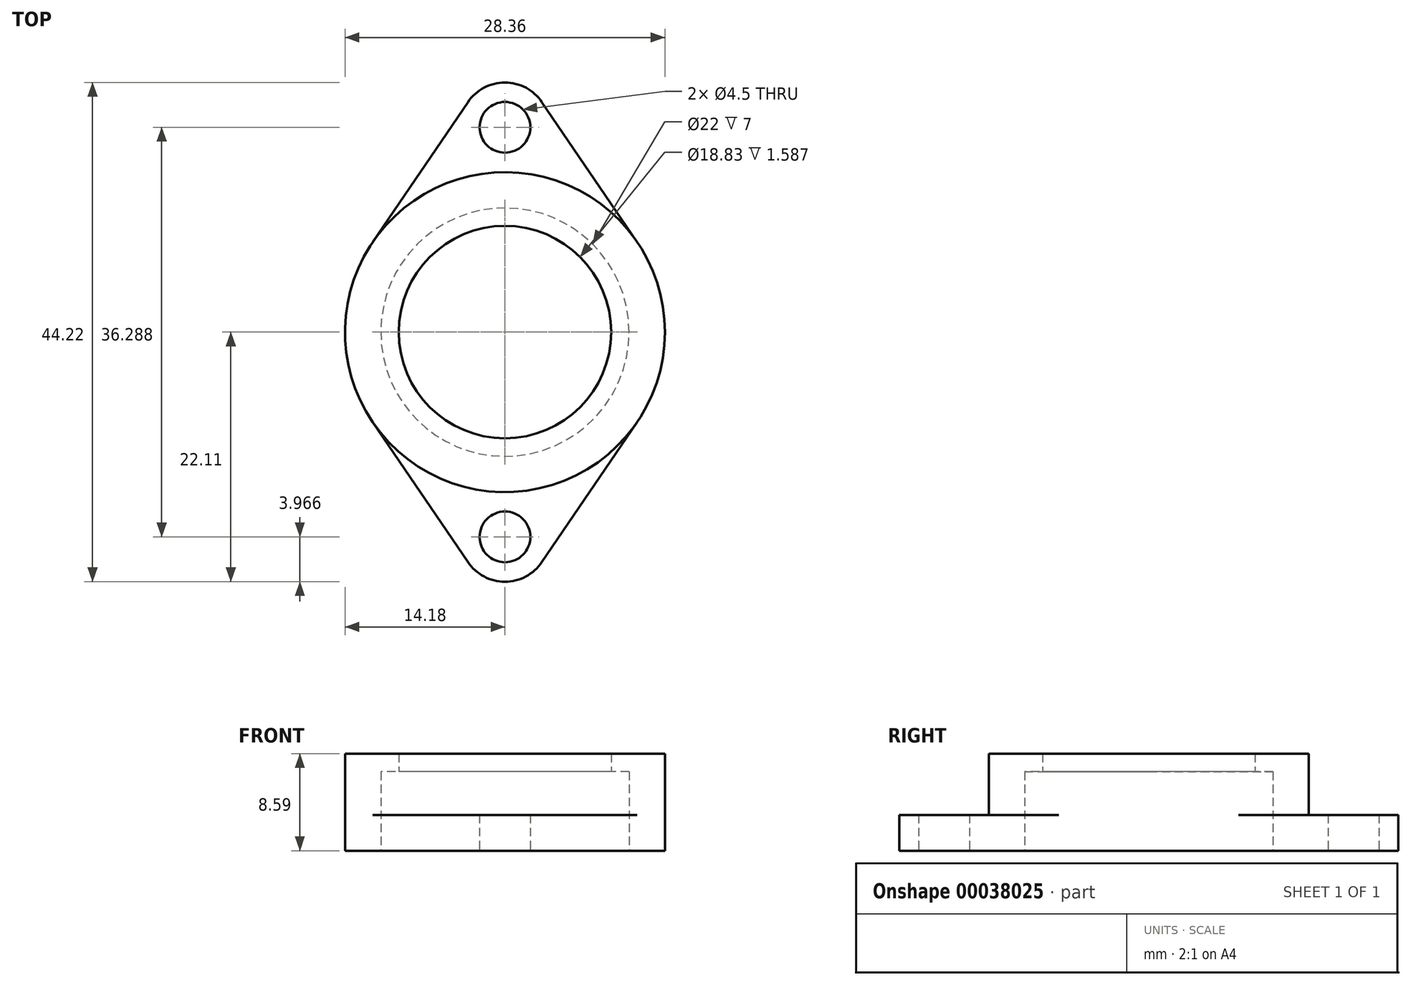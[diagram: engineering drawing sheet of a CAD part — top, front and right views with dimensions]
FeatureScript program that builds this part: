
annotation { "Feature Type Name" : "Feature", "Feature Type Description" : "" }
export const myFeature = defineFeature(function(context is Context, id is Id, definition is map)
    precondition{}
    {
        {
            var Q0;
            Q0=qCreatedBy(makeId("Top.planeOp"),FACE);
            var sketch = newSketch(context, id + "F0", { "sketchPlane" : qUnion([Q0])});
            skCircle(sketch, "E0", {"center": v(0, 0) * mm, "radius": 11 * mm});
            skArc(sketch, "E1", {"start": v(11.72, -7.97) * mm, "mid": v(14.18, 0) * mm, "end": v(11.72, 7.97) * mm});
            skArc(sketch, "E2", {"start": v(-11.72, 7.97) * mm, "mid": v(-14.18, 0) * mm, "end": v(-11.72, -7.97) * mm});
            skLineSegment(sketch, "E3", {"start": v(0, 18.14) * mm, "end": v(0, -18.14) * mm, "construction": true});
            skLineSegment(sketch, "E4", {"start": v(0, -18.14) * mm, "end": v(0, -18.14) * mm});
            skLineSegment(sketch, "E5", {"start": v(-3.97, 18.14) * mm, "end": v(3.97, 18.14) * mm, "construction": true});
            skLineSegment(sketch, "E6", {"start": v(-3.97, -18.14) * mm, "end": v(3.97, -18.14) * mm, "construction": true});
            skArc(sketch, "E7", {"start": v(-3.97, 18.14) * mm, "mid": v(0, 14.18) * mm, "end": v(3.97, 18.14) * mm, "construction": true});
            skArc(sketch, "E8", {"start": v(11.72, 7.97) * mm, "mid": v(0, 14.18) * mm, "end": v(-11.72, 7.97) * mm, "construction": true});
            skArc(sketch, "E9", {"start": v(3.28, 20.38) * mm, "mid": v(0, 22.11) * mm, "end": v(-3.28, 20.38) * mm});
            skLineSegment(sketch, "E10", {"start": v(-3.28, 20.38) * mm, "end": v(-11.72, 7.97) * mm});
            skArc(sketch, "E11", {"start": v(-3.28, 20.38) * mm, "mid": v(-3.8, 19.31) * mm, "end": v(-3.97, 18.14) * mm, "construction": true});
            skArc(sketch, "E12", {"start": v(3.97, 18.14) * mm, "mid": v(3.8, 19.31) * mm, "end": v(3.28, 20.38) * mm, "construction": true});
            skLineSegment(sketch, "E13", {"start": v(3.28, 20.38) * mm, "end": v(11.72, 7.97) * mm});
            skLineSegment(sketch, "E14", {"start": v(-11.72, -7.97) * mm, "end": v(-3.28, -20.38) * mm});
            skLineSegment(sketch, "E15", {"start": v(11.72, -7.97) * mm, "end": v(3.28, -20.38) * mm});
            skArc(sketch, "E16", {"start": v(-3.97, -18.14) * mm, "mid": v(-3.8, -19.31) * mm, "end": v(-3.28, -20.38) * mm, "construction": true});
            skArc(sketch, "E17", {"start": v(3.28, -20.38) * mm, "mid": v(3.8, -19.31) * mm, "end": v(3.97, -18.14) * mm, "construction": true});
            skArc(sketch, "E18", {"start": v(-3.28, -20.38) * mm, "mid": v(0, -22.11) * mm, "end": v(3.28, -20.38) * mm});
            skCircle(sketch, "E19", {"center": v(0, 18.14) * mm, "radius": 2.25 * mm});
            skCircle(sketch, "E20", {"center": v(0, -18.14) * mm, "radius": 2.25 * mm});
            skSolve(sketch);
        }
        {
            var Q0;
            Q0 = qSketchRegion(id + "F0", true);
            extrude(context, id + "F1", {"entities" : qUnion([Q0]), "depth" : 3.17 * mm});
        }
        {
            var Q0;
            Q0=makeQuery(id+"F1.opExtrude","CAP_FACE",FACE,{"disambiguationData":[OSD([sQuery(id+"F0.wireOp",EDGE,"E0"),sQuery(id+"F0.wireOp",EDGE,"E1"),sQuery(id+"F0.wireOp",EDGE,"E2"),sQuery(id+"F0.wireOp",EDGE,"E9"),sQuery(id+"F0.wireOp",EDGE,"E10"),sQuery(id+"F0.wireOp",EDGE,"E13"),sQuery(id+"F0.wireOp",EDGE,"E14"),sQuery(id+"F0.wireOp",EDGE,"E15"),sQuery(id+"F0.wireOp",EDGE,"E18"),sQuery(id+"F0.wireOp",EDGE,"E19"),sQuery(id+"F0.wireOp",EDGE,"E20")])],"isStart":false});
            var sketch = newSketch(context, id + "F2", { "sketchPlane" : qUnion([Q0])});
            skCircle(sketch, "E21", {"center": v(0, 0) * mm, "radius": 11 * mm});
            skCircle(sketch, "E22", {"center": v(0, 0) * mm, "radius": 14.18 * mm});
            skSolve(sketch);
        }
        {
            var Q0;
            Q0 = qSketchRegion(id + "F2", true);
            extrude(context, id + "F3", {"entities" : qUnion([Q0]), "operationType" : NewBodyOperationType.ADD, "depth" : 3.83 * mm});
        }
        {
            var Q0;
            Q0=makeQuery(id+"F3.opExtrude","CAP_FACE",FACE,{"disambiguationData":[OSD([sQuery(id+"F2.wireOp",EDGE,"E21"),sQuery(id+"F2.wireOp",EDGE,"E22")])],"isStart":false});
            var sketch = newSketch(context, id + "F4", { "sketchPlane" : qUnion([Q0])});
            skCircle(sketch, "E23", {"center": v(0, 0) * mm, "radius": 9.41 * mm});
            skCircle(sketch, "E24", {"center": v(0, 0) * mm, "radius": 14.18 * mm});
            skSolve(sketch);
        }
        {
            var Q0;
            Q0 = qSketchRegion(id + "F4", true);
            extrude(context, id + "F5", {"entities" : qUnion([Q0]), "operationType" : NewBodyOperationType.ADD, "depth" : 1.59 * mm});
        }
    });
